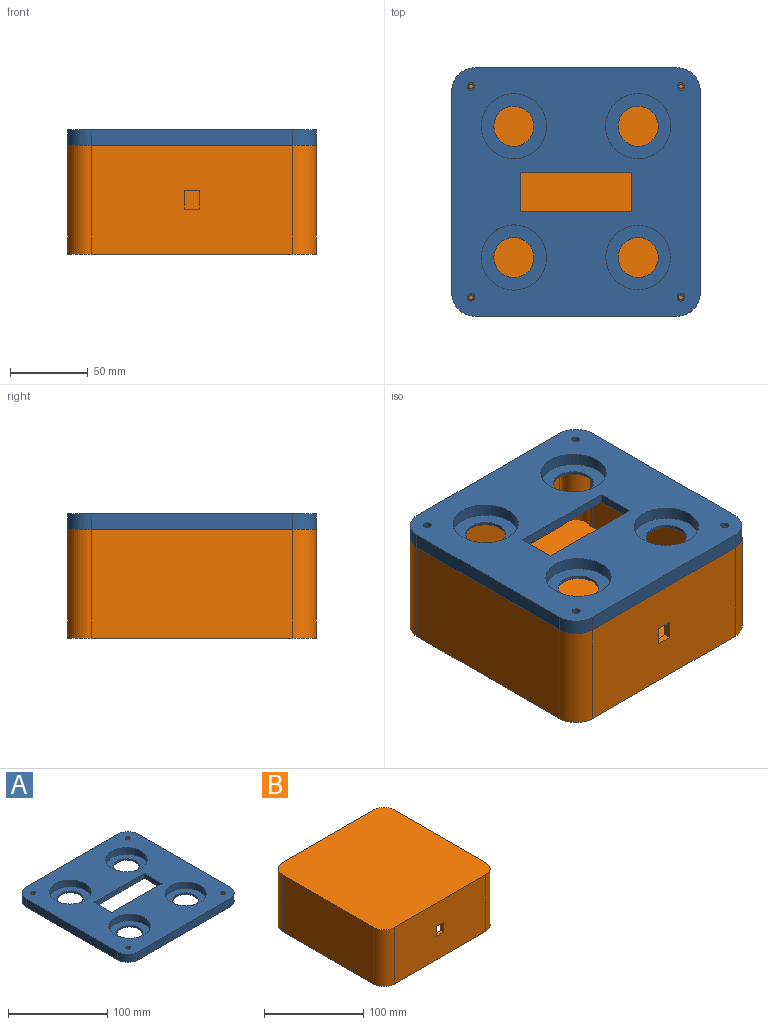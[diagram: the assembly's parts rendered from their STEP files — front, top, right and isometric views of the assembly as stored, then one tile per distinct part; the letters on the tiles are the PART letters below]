
ASSEMBLY  parts=2 mates=1
PART A: 53 faces, bbox 160x160x10 mm
  f0: plane 7x4.86mm, normal (0,-1,0), area 14.8mm2, adj f25,f44,f45,f46,f47,f52
  f1: plane 7x4.81mm, normal (0,1,0), area 14.7mm2, adj f2,f25,f44,f46,f48,f52
  f2: plane 25.5x6mm, normal (1,0,0), area 77.2mm2, adj f1,f3,f6,f24,f46,f52
  f3: plane 71.5x6mm, normal (0,-1,0), area 428.9mm2, adj f2,f23,f24,f45,f46,f52
  f4: cylinder r=21mm len=2.5mm, axis (0,0,-1), area 1.2mm2, adj f25,f30
  f5: cylinder r=21mm len=1.77mm, axis (0,0,-1), area 0.4mm2, adj f25,f29
  f6: plane 71.5x6mm, normal (0,1,0), area 429mm2, adj f2,f23,f24,f52
  f7: plane 130x10mm, normal (1,0,0), area 1300mm2, adj f8,f14,f24,f25
  f8: cylinder r=15mm len=15mm, axis (0,0,-1), area 235.6mm2, adj f7,f9,f24,f25
  f9: plane 130x10mm, normal (0,1,0), area 1300mm2, adj f8,f10,f24,f25
  f10: cylinder r=15mm len=15mm, axis (0,0,-1), area 235.6mm2, adj f9,f11,f24,f25
  f11: plane 130x10mm, normal (-1,0,0), area 1300mm2, adj f10,f12,f24,f25
  f12: cylinder r=15mm len=15mm, axis (0,0,-1), area 235.6mm2, adj f11,f13,f24,f25
  f13: plane 130x10mm, normal (0,-1,0), area 1300mm2, adj f12,f14,f24,f25
  f14: cylinder r=15mm len=15mm, axis (0,0,-1), area 235.6mm2, adj f7,f13,f24,f25
  f15: cylinder r=2.5mm len=5mm, axis (0,0,-1), area 39.3mm2, adj f24,f37
  f16: cylinder r=2.5mm len=5mm, axis (0,0,-1), area 39.3mm2, adj f24,f41
  f17: cylinder r=2.5mm len=5mm, axis (0,0,-1), area 39.3mm2, adj f24,f43
  f18: cylinder r=20.75mm len=41.5mm, axis (0,0,-1), area 1043mm2, adj f24,f34
  f19: cylinder r=21mm len=42mm, axis (0,0,-1), area 1055.6mm2, adj f24,f28
  f20: cylinder r=21mm len=42mm, axis (0,0,-1), area 1055.6mm2, adj f24,f26
  f21: cylinder r=21mm len=42mm, axis (0,0,-1), area 1055.6mm2, adj f24,f32
  f22: cylinder r=2.5mm len=5mm, axis (0,0,-1), area 39.3mm2, adj f24,f39
  f23: plane 25.5x6mm, normal (-1,0,0), area 153mm2, adj f3,f6,f24,f52
  f24: plane 160x160mm, normal (0,0,1), area 17996.1mm2, adj f2,f3,f6,f7,f8,f9,f10,f11
  f25: plane 160x160mm, normal (0,0,-1), area 20256.1mm2, adj f0,f1,f4,f5,f7,f8,f9,f10
  f26: plane 42x42mm, normal (0,0,1), area 863mm2, adj f20,f27
  f27: cone r=13mm half-angle=3deg, axis (0,0,-1), area 162.9mm2, adj f25,f26
  f28: plane 42x42mm, normal (0,0,1), area 863mm2, adj f19,f31
  f29: plane 1.77x0.36mm, normal (-0.04,-1,-0.05), area 0.4mm2, adj f5,f25
  f30: plane 2.5x0.71mm, normal (0.06,-1,-0.05), area 1.2mm2, adj f4,f25
  f31: cone r=13mm half-angle=3deg, axis (0,0,-1), area 162.9mm2, adj f25,f28
  f32: plane 42x42mm, normal (0,0,1), area 863mm2, adj f21,f33
  f33: cone r=13mm half-angle=3deg, axis (0,0,-1), area 162.9mm2, adj f25,f32
  f34: plane 41.5x41.5mm, normal (0,0,1), area 830.2mm2, adj f18,f35
  f35: cone r=13mm half-angle=3deg, axis (0,0,-1), area 162.9mm2, adj f25,f34
  f36: cylinder r=1.5mm len=7.5mm, axis (0,0,-1), area 70.7mm2, adj f25,f37
  f37: plane 5x5mm, normal (0,0,1), area 12.6mm2, adj f15,f36
  f38: cylinder r=1.5mm len=7.5mm, axis (0,0,-1), area 70.7mm2, adj f25,f39
  f39: plane 5x5mm, normal (0,0,1), area 12.6mm2, adj f22,f38
  f40: cylinder r=1.5mm len=7.5mm, axis (0,0,-1), area 70.7mm2, adj f25,f41
  f41: plane 5x5mm, normal (0,0,1), area 12.6mm2, adj f16,f40
  f42: cylinder r=1.5mm len=7.5mm, axis (0,0,-1), area 70.7mm2, adj f25,f43
  f43: plane 5x5mm, normal (0,0,1), area 12.6mm2, adj f17,f42
  f44: plane 25.33x7mm, normal (1,0,0), area 177.3mm2, adj f0,f1,f25,f46
  f45: plane 3x0.07mm, normal (-1,0,0), area 0.2mm2, adj f0,f3,f46,f52
  f46: plane 25.33x4.86mm, normal (0,0,-1), area 121.9mm2, adj f0,f1,f2,f3,f44,f45
  f47: plane 5.68x4mm, normal (1,0,0), area 22.7mm2, adj f0,f25,f51,f52
  f48: plane 5.99x4mm, normal (1,0,0), area 24mm2, adj f1,f25,f49,f52
  f49: plane 81x4mm, normal (0,1,0), area 324mm2, adj f25,f48,f50,f52
  f50: plane 37x4mm, normal (-1,0,0), area 148mm2, adj f25,f49,f51,f52
  f51: plane 81x4mm, normal (0,-1,0), area 324mm2, adj f25,f47,f50,f52
  f52: plane 81x37mm, normal (0,0,-1), area 1053.4mm2, adj f0,f1,f2,f3,f6,f23,f45,f47
PART B: 43 faces, bbox 160x160x70 mm
  f0: plane 122x60mm, normal (0,-1,0), area 7320mm2, adj f1,f15,f25,f42
  f1: cylinder r=15mm len=60mm, axis (0,0,-1), area 104.6mm2, adj f0,f2,f25,f30,f42
  f2: cylinder r=9.46mm len=30mm, axis (0,0,-1), area 742.8mm2, adj f1,f3,f32,f42
  f3: cylinder r=15mm len=60mm, axis (0,0,-1), area 130.7mm2, adj f2,f4,f25,f30,f42
  f4: plane 122x60mm, normal (-1,0,0), area 7320mm2, adj f3,f5,f25,f42
  f5: cylinder r=15mm len=60mm, axis (0,0,-1), area 130.7mm2, adj f4,f6,f25,f33,f42
  f6: cylinder r=9.46mm len=30mm, axis (0,0,-1), area 742.8mm2, adj f5,f7,f35,f42
  f7: cylinder r=15mm len=60mm, axis (0,0,-1), area 104.6mm2, adj f6,f8,f25,f33,f42
  f8: plane 122x60mm, normal (0,1,0), area 7200mm2, adj f7,f9,f25,f26,f27,f28,f29,f42
  f9: cylinder r=15mm len=60mm, axis (0,0,-1), area 104.6mm2, adj f8,f10,f25,f39,f42
  f10: cylinder r=9.46mm len=30mm, axis (0,0,-1), area 742.8mm2, adj f9,f11,f41,f42
  f11: cylinder r=15mm len=60mm, axis (0,0,-1), area 130.7mm2, adj f10,f12,f25,f39,f42
  f12: plane 122x60mm, normal (1,0,0), area 7320mm2, adj f11,f13,f25,f42
  f13: cylinder r=15mm len=60mm, axis (0,0,-1), area 130.7mm2, adj f12,f14,f25,f36,f42
  f14: cylinder r=9.46mm len=30mm, axis (0,0,-1), area 742.8mm2, adj f13,f15,f38,f42
  f15: cylinder r=15mm len=60mm, axis (0,0,-1), area 104.6mm2, adj f0,f14,f25,f36,f42
  f16: cylinder r=15mm len=70mm, axis (0,0,-1), area 1649.3mm2, adj f17,f23,f24,f25
  f17: plane 130x70mm, normal (0,1,0), area 9100mm2, adj f16,f18,f24,f25
  f18: cylinder r=15mm len=70mm, axis (0,0,-1), area 1649.3mm2, adj f17,f19,f24,f25
  f19: plane 130x70mm, normal (-1,0,0), area 9100mm2, adj f18,f20,f24,f25
  f20: cylinder r=15mm len=70mm, axis (0,0,-1), area 1649.3mm2, adj f19,f21,f24,f25
  f21: plane 130x70mm, normal (0,-1,0), area 8980mm2, adj f20,f22,f24,f25,f26,f27,f28,f29
  f22: cylinder r=15mm len=70mm, axis (0,0,-1), area 1649.3mm2, adj f21,f23,f24,f25
  f23: plane 130x70mm, normal (1,0,0), area 9100mm2, adj f16,f22,f24,f25
  f24: plane 160x160mm, normal (0,0,1), area 25406.9mm2, adj f16,f17,f18,f19,f20,f21,f22,f23
  f25: plane 160x160mm, normal (0,0,-1), area 3368.5mm2, adj f0,f1,f3,f4,f5,f7,f8,f9
  f26: plane 12x4mm, normal (1,0,0), area 48mm2, adj f8,f21,f27,f29
  f27: plane 10x4mm, normal (0,0,1), area 40mm2, adj f8,f21,f26,f28
  f28: plane 12x4mm, normal (-1,0,0), area 48mm2, adj f8,f21,f27,f29
  f29: plane 10x4mm, normal (0,0,-1), area 40mm2, adj f8,f21,f26,f28
  f30: cylinder r=9.46mm len=30mm, axis (0,0,-1), area 1039.4mm2, adj f1,f3,f25,f32
  f31: cylinder r=1.45mm len=30mm, axis (0,0,-1), area 273.3mm2, adj f25,f32
  f32: plane 18.91x18.91mm, normal (0,0,1), area 274.2mm2, adj f2,f30,f31
  f33: cylinder r=9.46mm len=30mm, axis (0,0,-1), area 1039.4mm2, adj f5,f7,f25,f35
  f34: cylinder r=1.45mm len=30mm, axis (0,0,-1), area 273.3mm2, adj f25,f35
  f35: plane 18.91x18.91mm, normal (0,0,1), area 274.2mm2, adj f6,f33,f34
  f36: cylinder r=9.46mm len=30mm, axis (0,0,-1), area 1039.4mm2, adj f13,f15,f25,f38
  f37: cylinder r=1.45mm len=30mm, axis (0,0,-1), area 273.3mm2, adj f25,f38
  f38: plane 18.91x18.91mm, normal (0,0,1), area 274.2mm2, adj f14,f36,f37
  f39: cylinder r=9.46mm len=30mm, axis (0,0,-1), area 1039.4mm2, adj f9,f11,f25,f41
  f40: cylinder r=1.45mm len=30mm, axis (0,0,-1), area 273.3mm2, adj f25,f41
  f41: plane 18.91x18.91mm, normal (0,0,1), area 274.2mm2, adj f10,f39,f40
  f42: plane 154.47x154.09mm, normal (0,0,-1), area 23135.3mm2, adj f0,f1,f2,f3,f4,f5,f6,f7
PLACE A t=(142.71,37.87,115.33)mm
PLACE B rot(axis=(0,1,0),180deg) t=(142.68,37.84,115.33)mm
MATE fastened A.f17 <-> B.f10  axis (0,0,-1) through (210.27,-29.95,115.33)mm
